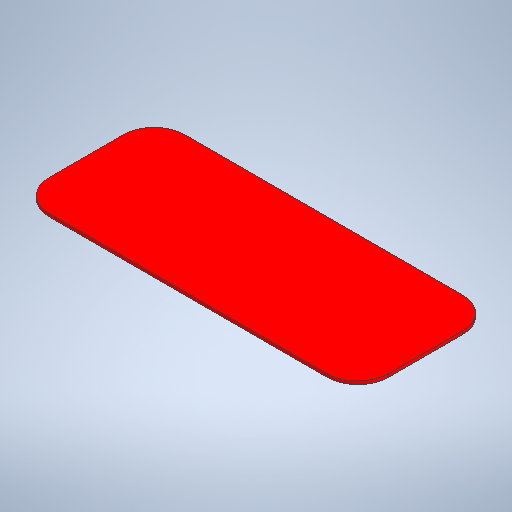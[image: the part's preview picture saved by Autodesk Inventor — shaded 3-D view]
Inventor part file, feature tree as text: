
AUTODESK INVENTOR PART (.ipt)
format: ipt  version: 2025.2 (Build 292293000, 293)  size: 238,592 bytes
history: native  units: mm
features: extrude x1, sketch x1
ambient origin geometry x8: Origin, YZ Plane, XZ Plane, XY Plane, X Axis, Y Axis, Z Axis, Center Point
bodies: Solid1 (feature_tree)
feature tree (2):
  extrude  "Extrusion1"  Depth=44.0mm
  sketch  "Sketch1"  dims[d0=110.0mm d1=44.0mm d2=10.0mm d3=10.0mm d4=10.0mm d5=1.0mm d6=0.0mm]
